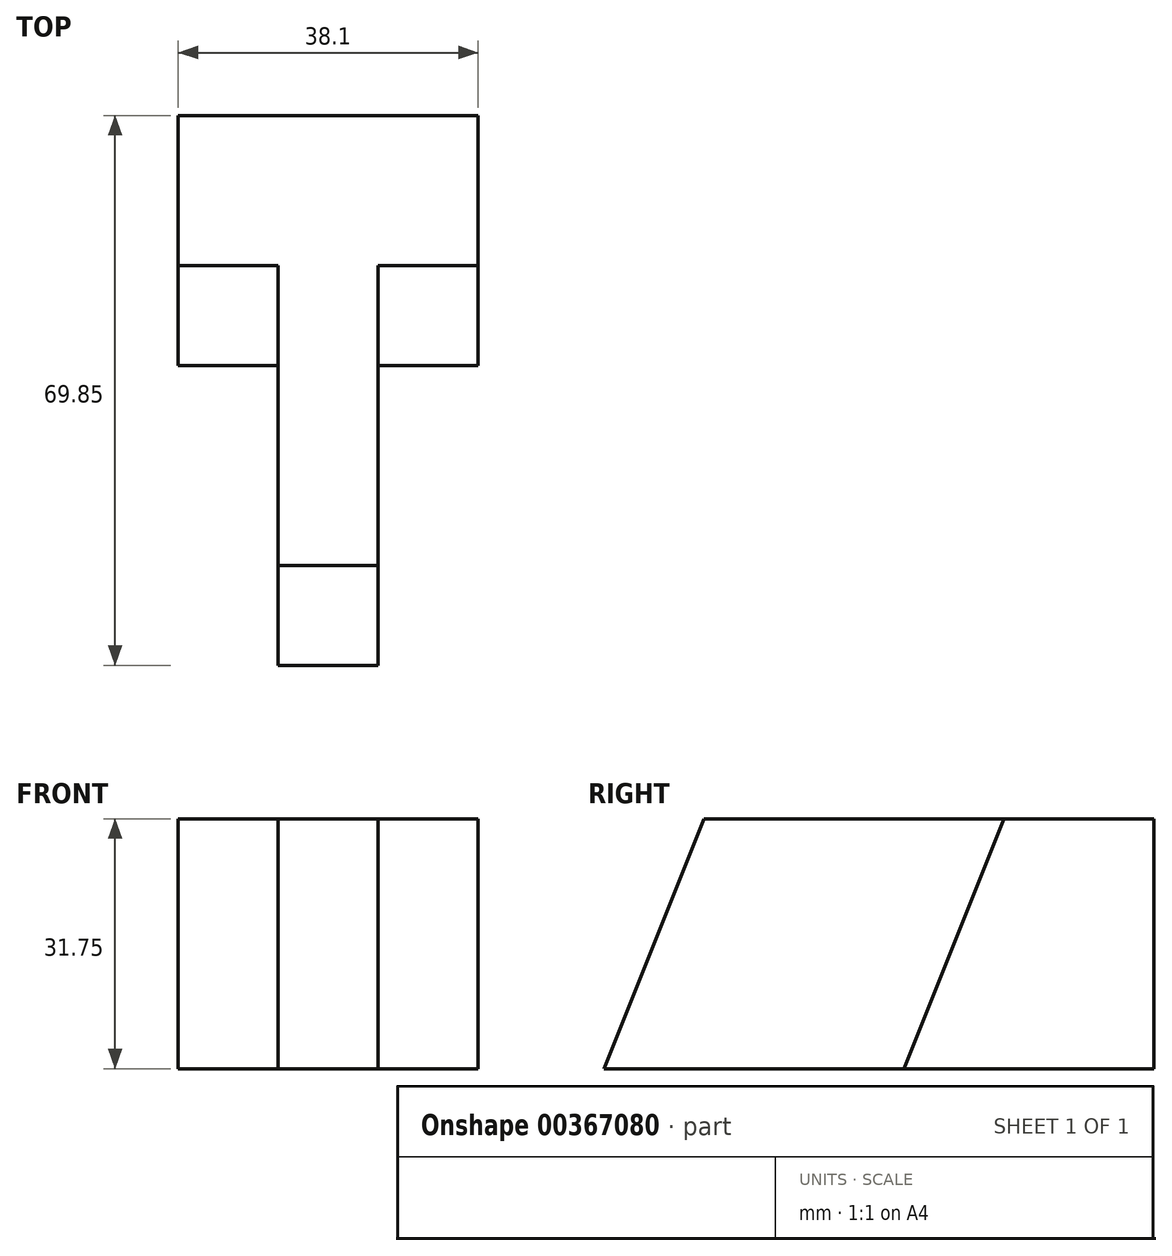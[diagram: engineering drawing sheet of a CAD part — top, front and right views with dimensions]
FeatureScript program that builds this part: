
annotation { "Feature Type Name" : "Feature", "Feature Type Description" : "" }
export const myFeature = defineFeature(function(context is Context, id is Id, definition is map)
    precondition{}
    {
        {
            var Q0;
            Q0=qCreatedBy(makeId("Top.planeOp"),FACE);
            var sketch = newSketch(context, id + "F0", { "sketchPlane" : qUnion([Q0])});
            skLineSegment(sketch, "E0", {"start": v(0, 0) * mm, "end": v(0, 38.1) * mm});
            skLineSegment(sketch, "E1", {"start": v(0, 38.1) * mm, "end": v(-12.7, 38.1) * mm});
            skLineSegment(sketch, "E2", {"start": v(-12.7, 38.1) * mm, "end": v(-12.7, 69.85) * mm});
            skLineSegment(sketch, "E3", {"start": v(-12.7, 69.85) * mm, "end": v(25.4, 69.85) * mm});
            skLineSegment(sketch, "E4", {"start": v(25.4, 69.85) * mm, "end": v(25.4, 38.1) * mm});
            skLineSegment(sketch, "E5", {"start": v(25.4, 38.1) * mm, "end": v(12.7, 38.1) * mm});
            skLineSegment(sketch, "E6", {"start": v(12.7, 38.1) * mm, "end": v(12.7, 0) * mm});
            skLineSegment(sketch, "E7", {"start": v(12.7, 0) * mm, "end": v(0, 0) * mm});
            skSolve(sketch);
        }
        {
            var Q0;
            Q0=makeQuery(id+"F0.imprint","IMPRINT",FACE,{"disambiguationData":[TD([[makeQuery(id+"F0.imprint","IMPRINT",EDGE,{"derivedFrom":sQuery(id+"F0.wireOp",EDGE,"E0")}),-1.0]])]});
            extrude(context, id + "F1", {"entities" : qUnion([Q0]), "depth" : 31.75 * mm});
        }
        {
            var Q0;
            Q0=qCreatedBy(makeId("Right.planeOp"),FACE);
            var sketch = newSketch(context, id + "F2", { "sketchPlane" : qUnion([Q0])});
            skLineSegment(sketch, "E8", {"start": v(0, 0) * mm, "end": v(0, 31.75) * mm});
            skLineSegment(sketch, "E9", {"start": v(0, 31.75) * mm, "end": v(12.7, 31.75) * mm});
            skLineSegment(sketch, "E10", {"start": v(12.7, 31.75) * mm, "end": v(0, 0) * mm});
            skSolve(sketch);
        }
        {
            var Q0;
            Q0 = qSketchRegion(id + "F2", true);
            extrude(context, id + "F3", {"entities" : qUnion([Q0]), "operationType" : NewBodyOperationType.REMOVE, "depth" : 25.4 * mm});
        }
        {
            var Q0;
            Q0=qCreatedBy(makeId("Right.planeOp"),FACE);
            var sketch = newSketch(context, id + "F4", { "sketchPlane" : qUnion([Q0])});
            skLineSegment(sketch, "E11", {"start": v(38.1, 31.75) * mm, "end": v(50.8, 31.75) * mm});
            skLineSegment(sketch, "E12", {"start": v(50.8, 31.75) * mm, "end": v(38.1, 0) * mm});
            skLineSegment(sketch, "E13", {"start": v(38.1, 0) * mm, "end": v(38.1, 31.75) * mm});
            skSolve(sketch);
        }
        {
            var Q0;
            Q0 = qSketchRegion(id + "F4", true);
            extrude(context, id + "F5", {"entities" : qUnion([Q0]), "operationType" : NewBodyOperationType.REMOVE, "oppositeDirection" : true, "depth" : 12.7 * mm});
        }
        {
            var Q0;
            Q0=qCreatedBy(makeId("Right.planeOp"),FACE);
            var sketch = newSketch(context, id + "F6", { "sketchPlane" : qUnion([Q0])});
            skLineSegment(sketch, "E14", {"start": v(38.1, 31.75) * mm, "end": v(38.1, 0) * mm});
            skLineSegment(sketch, "E15", {"start": v(38.1, 0) * mm, "end": v(50.8, 31.75) * mm});
            skLineSegment(sketch, "E16", {"start": v(50.8, 31.75) * mm, "end": v(38.1, 31.75) * mm});
            skSolve(sketch);
        }
        {
            var Q0;
            Q0 = qSketchRegion(id + "F6", true);
            extrude(context, id + "F7", {"entities" : qUnion([Q0]), "operationType" : NewBodyOperationType.REMOVE, "depth" : 25.4 * mm});
        }
        {
            var Q0;
            Q0=qCreatedBy(makeId("Right.planeOp"),FACE);
            var sketch = newSketch(context, id + "F8", { "sketchPlane" : qUnion([Q0])});
            skLineSegment(sketch, "E17", {"start": v(50.8, 31.75) * mm, "end": v(38.1, 31.75) * mm});
            skLineSegment(sketch, "E18", {"start": v(38.1, 31.75) * mm, "end": v(38.1, 0) * mm});
            skLineSegment(sketch, "E19", {"start": v(38.1, 0) * mm, "end": v(50.8, 31.75) * mm});
            skSolve(sketch);
        }
        {
            var Q0;
            Q0 = qSketchRegion(id + "F8", true);
            extrude(context, id + "F9", {"entities" : qUnion([Q0]), "operationType" : NewBodyOperationType.ADD, "depth" : 12.7 * mm});
        }
    });
